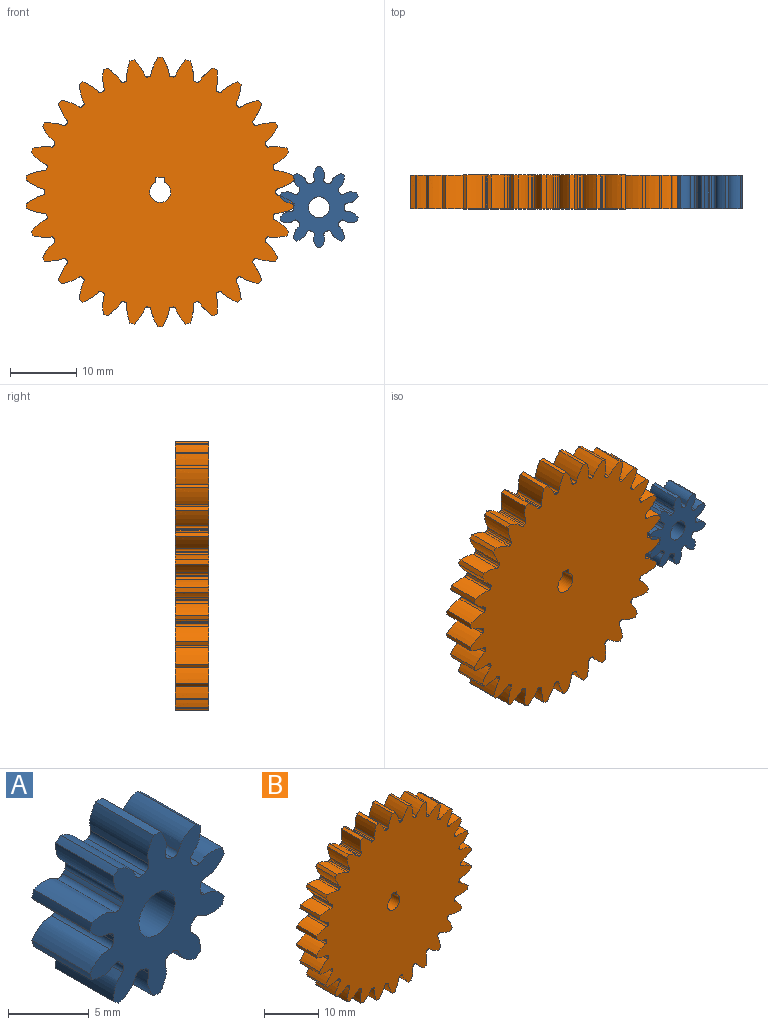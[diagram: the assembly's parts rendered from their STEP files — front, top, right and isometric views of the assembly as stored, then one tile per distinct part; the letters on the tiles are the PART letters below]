
ASSEMBLY  parts=2 mates=1
PART A: 63 faces, bbox 11.8x5.1x12.2 mm
  f0: cylinder r=6.1mm len=5.08mm, axis (0,1,0), area 3mm2, adj f9,f11,f52,f59
  f1: cylinder r=6.1mm len=5.08mm, axis (0,1,0), area 3mm2, adj f9,f11,f12,f54
  f2: cylinder r=6.1mm len=5.08mm, axis (0,1,0), area 3mm2, adj f9,f11,f42,f49
  f3: cylinder r=6.1mm len=5.08mm, axis (0,1,0), area 3mm2, adj f9,f11,f44,f57
  f4: cylinder r=6.1mm len=5.08mm, axis (0,1,0), area 3mm2, adj f9,f11,f32,f39
  f5: cylinder r=6.1mm len=5.08mm, axis (0,1,0), area 3mm2, adj f9,f11,f27,f34
  f6: cylinder r=6.1mm len=5.08mm, axis (0,1,0), area 3mm2, adj f9,f11,f22,f29
  f7: cylinder r=6.1mm len=5.08mm, axis (0,1,0), area 3mm2, adj f9,f11,f24,f47
  f8: cylinder r=6.1mm len=5.08mm, axis (0,1,0), area 3mm2, adj f9,f11,f19,f37
  f9: plane 12.21x11.79mm, normal (0,-1,0), area 69.6mm2, adj f0,f1,f2,f3,f4,f5,f6,f7
  f10: cylinder r=6.1mm len=5.08mm, axis (0,1,0), area 3mm2, adj f9,f11,f14,f17
  f11: plane 12.21x11.79mm, normal (0,1,0), area 69.6mm2, adj f0,f1,f2,f3,f4,f5,f6,f7
  f12: extruded ~5.08x1.72mm, area 10.5mm2, adj f1,f9,f11,f15
  f13: cylinder r=3.81mm len=5.08mm, axis (0,1,0), area 1.7mm2, adj f9,f11,f15,f16
  f14: extruded ~5.08x1.72mm, area 10.5mm2, adj f9,f10,f11,f16
  f15: cylinder r=0.42mm len=5.08mm, axis (0,1,0), area 3.1mm2, adj f9,f11,f12,f13
  f16: cylinder r=0.42mm len=5.08mm, axis (0,1,0), area 3.1mm2, adj f9,f11,f13,f14
  f17: extruded ~5.08x1.98mm, area 10.5mm2, adj f9,f10,f11,f20
  f18: cylinder r=3.81mm len=5.08mm, axis (0,1,0), area 1.7mm2, adj f9,f11,f20,f21
  f19: extruded ~5.08x1.82mm, area 10.5mm2, adj f8,f9,f11,f21
  f20: cylinder r=0.42mm len=5.08mm, axis (0,1,0), area 3.1mm2, adj f9,f11,f17,f18
  f21: cylinder r=0.42mm len=5.08mm, axis (0,1,0), area 3.1mm2, adj f9,f11,f18,f19
  f22: extruded ~5.08x1.72mm, area 10.5mm2, adj f6,f9,f11,f25
  f23: cylinder r=3.81mm len=5.08mm, axis (0,1,0), area 1.7mm2, adj f9,f11,f25,f26
  f24: extruded ~5.08x1.72mm, area 10.5mm2, adj f7,f9,f11,f26
  f25: cylinder r=0.42mm len=5.08mm, axis (0,1,0), area 3.1mm2, adj f9,f11,f22,f23
  f26: cylinder r=0.42mm len=5.08mm, axis (0,1,0), area 3.1mm2, adj f9,f11,f23,f24
  f27: extruded ~5.08x1.82mm, area 10.5mm2, adj f5,f9,f11,f30
  f28: cylinder r=3.81mm len=5.08mm, axis (0,1,0), area 1.7mm2, adj f9,f11,f30,f31
  f29: extruded ~5.08x1.98mm, area 10.5mm2, adj f6,f9,f11,f31
  f30: cylinder r=0.42mm len=5.08mm, axis (0,1,0), area 3.1mm2, adj f9,f11,f27,f28
  f31: cylinder r=0.42mm len=5.08mm, axis (0,1,0), area 3.1mm2, adj f9,f11,f28,f29
  f32: extruded ~5.08x1.94mm, area 10.5mm2, adj f4,f9,f11,f35
  f33: cylinder r=3.81mm len=5.08mm, axis (0,1,0), area 1.7mm2, adj f9,f11,f35,f36
  f34: extruded ~5.08x1.48mm, area 10.5mm2, adj f5,f9,f11,f36
  f35: cylinder r=0.42mm len=5.08mm, axis (0,1,0), area 3.1mm2, adj f9,f11,f32,f33
  f36: cylinder r=0.42mm len=5.08mm, axis (0,1,0), area 3.1mm2, adj f9,f11,f33,f34
  f37: extruded ~5.08x1.48mm, area 10.5mm2, adj f8,f9,f11,f40
  f38: cylinder r=3.81mm len=5.08mm, axis (0,1,0), area 1.7mm2, adj f9,f11,f40,f41
  f39: extruded ~5.08x1.94mm, area 10.5mm2, adj f4,f9,f11,f41
  f40: cylinder r=0.42mm len=5.08mm, axis (0,1,0), area 3.1mm2, adj f9,f11,f37,f38
  f41: cylinder r=0.42mm len=5.08mm, axis (0,1,0), area 3.1mm2, adj f9,f11,f38,f39
  f42: extruded ~5.08x1.48mm, area 10.5mm2, adj f2,f9,f11,f45
  f43: cylinder r=3.81mm len=5.08mm, axis (0,1,0), area 1.7mm2, adj f9,f11,f45,f46
  f44: extruded ~5.08x1.94mm, area 10.5mm2, adj f3,f9,f11,f46
  f45: cylinder r=0.42mm len=5.08mm, axis (0,1,0), area 3.1mm2, adj f9,f11,f42,f43
  f46: cylinder r=0.42mm len=5.08mm, axis (0,1,0), area 3.1mm2, adj f9,f11,f43,f44
  f47: extruded ~5.08x1.98mm, area 10.5mm2, adj f7,f9,f11,f50
  f48: cylinder r=3.81mm len=5.08mm, axis (0,1,0), area 1.7mm2, adj f9,f11,f50,f51
  f49: extruded ~5.08x1.82mm, area 10.5mm2, adj f2,f9,f11,f51
  f50: cylinder r=0.42mm len=5.08mm, axis (0,1,0), area 3.1mm2, adj f9,f11,f47,f48
  f51: cylinder r=0.42mm len=5.08mm, axis (0,1,0), area 3.1mm2, adj f9,f11,f48,f49
  f52: extruded ~5.08x1.82mm, area 10.5mm2, adj f0,f9,f11,f55
  f53: cylinder r=3.81mm len=5.08mm, axis (0,1,0), area 1.7mm2, adj f9,f11,f55,f56
  f54: extruded ~5.08x1.98mm, area 10.5mm2, adj f1,f9,f11,f56
  f55: cylinder r=0.42mm len=5.08mm, axis (0,1,0), area 3.1mm2, adj f9,f11,f52,f53
  f56: cylinder r=0.42mm len=5.08mm, axis (0,1,0), area 3.1mm2, adj f9,f11,f53,f54
  f57: extruded ~5.08x1.94mm, area 10.5mm2, adj f3,f9,f11,f60
  f58: cylinder r=3.81mm len=5.08mm, axis (0,1,0), area 1.7mm2, adj f9,f11,f60,f61
  f59: extruded ~5.08x1.48mm, area 10.5mm2, adj f0,f9,f11,f61
  f60: cylinder r=0.42mm len=5.08mm, axis (0,1,0), area 3.1mm2, adj f9,f11,f57,f58
  f61: cylinder r=0.42mm len=5.08mm, axis (0,1,0), area 3.1mm2, adj f9,f11,f58,f59
  f62: cylinder r=1.59mm len=5.08mm, axis (0,1,0), area 50.7mm2, adj f9,f11
PART B: 186 faces, bbox 40.5x5.1x40.6 mm
  f0: cylinder r=20.32mm len=5.08mm, axis (0,1,0), area 3.5mm2, adj f29,f35,f176,f183
  f1: cylinder r=20.32mm len=5.08mm, axis (0,1,0), area 3.5mm2, adj f29,f35,f171,f178
  f2: cylinder r=20.32mm len=5.08mm, axis (0,1,0), area 3.5mm2, adj f29,f35,f166,f173
  f3: cylinder r=20.32mm len=5.08mm, axis (0,1,0), area 3.5mm2, adj f29,f35,f156,f168
  f4: cylinder r=20.32mm len=5.08mm, axis (0,1,0), area 3.5mm2, adj f29,f35,f151,f163
  f5: cylinder r=20.32mm len=5.08mm, axis (0,1,0), area 3.5mm2, adj f29,f35,f158,f161
  f6: cylinder r=20.32mm len=5.08mm, axis (0,1,0), area 3.5mm2, adj f29,f35,f146,f153
  f7: cylinder r=20.32mm len=5.08mm, axis (0,1,0), area 3.5mm2, adj f29,f35,f36,f148
  f8: cylinder r=20.32mm len=5.08mm, axis (0,1,0), area 3.5mm2, adj f29,f35,f131,f143
  f9: cylinder r=20.32mm len=5.08mm, axis (0,1,0), area 3.5mm2, adj f29,f35,f138,f141
  f10: cylinder r=20.32mm len=5.08mm, axis (0,1,0), area 3.5mm2, adj f29,f35,f126,f133
  f11: cylinder r=20.32mm len=5.08mm, axis (0,1,0), area 3.5mm2, adj f29,f35,f128,f181
  f12: cylinder r=20.32mm len=5.08mm, axis (0,1,0), area 3.5mm2, adj f29,f35,f123,f136
  f13: cylinder r=20.32mm len=5.08mm, axis (0,1,0), area 3.5mm2, adj f29,f35,f118,f121
  f14: cylinder r=20.32mm len=5.08mm, axis (0,1,0), area 3.5mm2, adj f29,f35,f113,f116
  f15: cylinder r=20.32mm len=5.08mm, axis (0,1,0), area 3.5mm2, adj f29,f35,f108,f111
  f16: cylinder r=20.32mm len=5.08mm, axis (0,1,0), area 3.5mm2, adj f29,f35,f91,f103
  f17: cylinder r=20.32mm len=5.08mm, axis (0,1,0), area 3.5mm2, adj f29,f35,f98,f101
  f18: cylinder r=20.32mm len=5.08mm, axis (0,1,0), area 3.5mm2, adj f29,f35,f86,f93
  f19: cylinder r=20.32mm len=5.08mm, axis (0,1,0), area 3.5mm2, adj f29,f35,f88,f106
  f20: cylinder r=20.32mm len=5.08mm, axis (0,1,0), area 3.5mm2, adj f29,f35,f83,f96
  f21: cylinder r=20.32mm len=5.08mm, axis (0,1,0), area 3.5mm2, adj f29,f35,f78,f81
  f22: cylinder r=20.32mm len=5.08mm, axis (0,1,0), area 3.5mm2, adj f29,f35,f73,f76
  f23: cylinder r=20.32mm len=5.08mm, axis (0,1,0), area 3.5mm2, adj f29,f35,f68,f71
  f24: cylinder r=20.32mm len=5.08mm, axis (0,1,0), area 3.5mm2, adj f29,f35,f56,f63
  f25: cylinder r=20.32mm len=5.08mm, axis (0,1,0), area 3.5mm2, adj f29,f35,f46,f58
  f26: cylinder r=20.32mm len=5.08mm, axis (0,1,0), area 3.5mm2, adj f29,f35,f53,f66
  f27: cylinder r=20.32mm len=5.08mm, axis (0,1,0), area 3.5mm2, adj f29,f35,f48,f51
  f28: cylinder r=20.32mm len=5.08mm, axis (0,1,0), area 3.5mm2, adj f29,f35,f43,f61
  f29: plane 40.64x40.49mm, normal (0,-1,0), area 1122.1mm2, adj f0,f1,f2,f3,f4,f5,f6,f7
  f30: plane 5.08x0.77mm, normal (-1,0,0), area 3.9mm2, adj f29,f31,f33,f35
  f31: cylinder r=1.59mm len=5.08mm, axis (0,1,0), area 44mm2, adj f29,f30,f32,f35
  f32: plane 5.08x0.77mm, normal (1,0,0), area 3.9mm2, adj f29,f31,f33,f35
  f33: plane 5.08x1.27mm, normal (0,0,-1), area 6.5mm2, adj f29,f30,f32,f35
  f34: cylinder r=20.32mm len=5.08mm, axis (0,1,0), area 3.5mm2, adj f29,f35,f38,f41
  f35: plane 40.64x40.49mm, normal (0,1,0), area 1122.1mm2, adj f0,f1,f2,f3,f4,f5,f6,f7
  f36: extruded ~5.08x2.52mm, area 14.5mm2, adj f7,f29,f35,f39
  f37: cylinder r=17.46mm len=5.08mm, axis (0,1,0), area 1.3mm2, adj f29,f35,f39,f40
  f38: extruded ~5.08x2.52mm, area 14.5mm2, adj f29,f34,f35,f40
  f39: cylinder r=0.35mm len=5.08mm, axis (0,1,0), area 2.3mm2, adj f29,f35,f36,f37
  f40: cylinder r=0.35mm len=5.08mm, axis (0,1,0), area 2.3mm2, adj f29,f35,f37,f38
  f41: extruded ~5.08x2.74mm, area 14.5mm2, adj f29,f34,f35,f44
  f42: cylinder r=17.46mm len=5.08mm, axis (0,1,0), area 1.3mm2, adj f29,f35,f44,f45
  f43: extruded ~5.08x2.19mm, area 14.5mm2, adj f28,f29,f35,f45
  f44: cylinder r=0.35mm len=5.08mm, axis (0,1,0), area 2.3mm2, adj f29,f35,f41,f42
  f45: cylinder r=0.35mm len=5.08mm, axis (0,1,0), area 2.3mm2, adj f29,f35,f42,f43
  f46: extruded ~5.08x2.66mm, area 14.5mm2, adj f25,f29,f35,f49
  f47: cylinder r=17.46mm len=5.08mm, axis (0,1,0), area 1.3mm2, adj f29,f35,f49,f50
  f48: extruded ~5.08x2.75mm, area 14.5mm2, adj f27,f29,f35,f50
  f49: cylinder r=0.35mm len=5.08mm, axis (0,1,0), area 2.3mm2, adj f29,f35,f46,f47
  f50: cylinder r=0.35mm len=5.08mm, axis (0,1,0), area 2.3mm2, adj f29,f35,f47,f48
  f51: extruded ~5.08x2.39mm, area 14.5mm2, adj f27,f29,f35,f54
  f52: cylinder r=17.46mm len=5.08mm, axis (0,1,0), area 1.3mm2, adj f29,f35,f54,f55
  f53: extruded ~5.08x2.84mm, area 14.5mm2, adj f26,f29,f35,f55
  f54: cylinder r=0.35mm len=5.08mm, axis (0,1,0), area 2.3mm2, adj f29,f35,f51,f52
  f55: cylinder r=0.35mm len=5.08mm, axis (0,1,0), area 2.3mm2, adj f29,f35,f52,f53
  f56: extruded ~5.08x2.81mm, area 14.5mm2, adj f24,f29,f35,f59
  f57: cylinder r=17.46mm len=5.08mm, axis (0,1,0), area 1.3mm2, adj f29,f35,f59,f60
  f58: extruded ~5.08x2.54mm, area 14.5mm2, adj f25,f29,f35,f60
  f59: cylinder r=0.35mm len=5.08mm, axis (0,1,0), area 2.3mm2, adj f29,f35,f56,f57
  f60: cylinder r=0.35mm len=5.08mm, axis (0,1,0), area 2.3mm2, adj f29,f35,f57,f58
  f61: extruded ~5.08x2.83mm, area 14.5mm2, adj f28,f29,f35,f64
  f62: cylinder r=17.46mm len=5.08mm, axis (0,1,0), area 1.3mm2, adj f29,f35,f64,f65
  f63: extruded ~5.08x2.22mm, area 14.5mm2, adj f24,f29,f35,f65
  f64: cylinder r=0.35mm len=5.08mm, axis (0,1,0), area 2.3mm2, adj f29,f35,f61,f62
  f65: cylinder r=0.35mm len=5.08mm, axis (0,1,0), area 2.3mm2, adj f29,f35,f62,f63
  f66: extruded ~5.08x2.02mm, area 14.5mm2, adj f26,f29,f35,f69
  f67: cylinder r=17.46mm len=5.08mm, axis (0,1,0), area 1.3mm2, adj f29,f35,f69,f70
  f68: extruded ~5.08x2.8mm, area 14.5mm2, adj f23,f29,f35,f70
  f69: cylinder r=0.35mm len=5.08mm, axis (0,1,0), area 2.3mm2, adj f29,f35,f66,f67
  f70: cylinder r=0.35mm len=5.08mm, axis (0,1,0), area 2.3mm2, adj f29,f35,f67,f68
  f71: extruded ~5.08x2.37mm, area 14.5mm2, adj f23,f29,f35,f74
  f72: cylinder r=17.46mm len=5.08mm, axis (0,1,0), area 1.3mm2, adj f29,f35,f74,f75
  f73: extruded ~5.08x2.64mm, area 14.5mm2, adj f22,f29,f35,f75
  f74: cylinder r=0.35mm len=5.08mm, axis (0,1,0), area 2.3mm2, adj f29,f35,f71,f72
  f75: cylinder r=0.35mm len=5.08mm, axis (0,1,0), area 2.3mm2, adj f29,f35,f72,f73
  f76: extruded ~5.08x2.64mm, area 14.5mm2, adj f22,f29,f35,f79
  f77: cylinder r=17.46mm len=5.08mm, axis (0,1,0), area 1.3mm2, adj f29,f35,f79,f80
  f78: extruded ~5.08x2.37mm, area 14.5mm2, adj f21,f29,f35,f80
  f79: cylinder r=0.35mm len=5.08mm, axis (0,1,0), area 2.3mm2, adj f29,f35,f76,f77
  f80: cylinder r=0.35mm len=5.08mm, axis (0,1,0), area 2.3mm2, adj f29,f35,f77,f78
  f81: extruded ~5.08x2.8mm, area 14.5mm2, adj f21,f29,f35,f84
  f82: cylinder r=17.46mm len=5.08mm, axis (0,1,0), area 1.3mm2, adj f29,f35,f84,f85
  f83: extruded ~5.08x2.02mm, area 14.5mm2, adj f20,f29,f35,f85
  f84: cylinder r=0.35mm len=5.08mm, axis (0,1,0), area 2.3mm2, adj f29,f35,f81,f82
  f85: cylinder r=0.35mm len=5.08mm, axis (0,1,0), area 2.3mm2, adj f29,f35,f82,f83
  f86: extruded ~5.08x2.22mm, area 14.5mm2, adj f18,f29,f35,f89
  f87: cylinder r=17.46mm len=5.08mm, axis (0,1,0), area 1.3mm2, adj f29,f35,f89,f90
  f88: extruded ~5.08x2.83mm, area 14.5mm2, adj f19,f29,f35,f90
  f89: cylinder r=0.35mm len=5.08mm, axis (0,1,0), area 2.3mm2, adj f29,f35,f86,f87
  f90: cylinder r=0.35mm len=5.08mm, axis (0,1,0), area 2.3mm2, adj f29,f35,f87,f88
  f91: extruded ~5.08x2.54mm, area 14.5mm2, adj f16,f29,f35,f94
  f92: cylinder r=17.46mm len=5.08mm, axis (0,1,0), area 1.3mm2, adj f29,f35,f94,f95
  f93: extruded ~5.08x2.81mm, area 14.5mm2, adj f18,f29,f35,f95
  f94: cylinder r=0.35mm len=5.08mm, axis (0,1,0), area 2.3mm2, adj f29,f35,f91,f92
  f95: cylinder r=0.35mm len=5.08mm, axis (0,1,0), area 2.3mm2, adj f29,f35,f92,f93
  f96: extruded ~5.08x2.84mm, area 14.5mm2, adj f20,f29,f35,f99
  f97: cylinder r=17.46mm len=5.08mm, axis (0,1,0), area 1.3mm2, adj f29,f35,f99,f100
  f98: extruded ~5.08x2.39mm, area 14.5mm2, adj f17,f29,f35,f100
  f99: cylinder r=0.35mm len=5.08mm, axis (0,1,0), area 2.3mm2, adj f29,f35,f96,f97
  f100: cylinder r=0.35mm len=5.08mm, axis (0,1,0), area 2.3mm2, adj f29,f35,f97,f98
  f101: extruded ~5.08x2.75mm, area 14.5mm2, adj f17,f29,f35,f104
  f102: cylinder r=17.46mm len=5.08mm, axis (0,1,0), area 1.3mm2, adj f29,f35,f104,f105
  f103: extruded ~5.08x2.66mm, area 14.5mm2, adj f16,f29,f35,f105
  f104: cylinder r=0.35mm len=5.08mm, axis (0,1,0), area 2.3mm2, adj f29,f35,f101,f102
  f105: cylinder r=0.35mm len=5.08mm, axis (0,1,0), area 2.3mm2, adj f29,f35,f102,f103
  f106: extruded ~5.08x2.19mm, area 14.5mm2, adj f19,f29,f35,f109
  f107: cylinder r=17.46mm len=5.08mm, axis (0,1,0), area 1.3mm2, adj f29,f35,f109,f110
  f108: extruded ~5.08x2.74mm, area 14.5mm2, adj f15,f29,f35,f110
  f109: cylinder r=0.35mm len=5.08mm, axis (0,1,0), area 2.3mm2, adj f29,f35,f106,f107
  f110: cylinder r=0.35mm len=5.08mm, axis (0,1,0), area 2.3mm2, adj f29,f35,f107,f108
  f111: extruded ~5.08x2.52mm, area 14.5mm2, adj f15,f29,f35,f114
  f112: cylinder r=17.46mm len=5.08mm, axis (0,1,0), area 1.3mm2, adj f29,f35,f114,f115
  f113: extruded ~5.08x2.52mm, area 14.5mm2, adj f14,f29,f35,f115
  f114: cylinder r=0.35mm len=5.08mm, axis (0,1,0), area 2.3mm2, adj f29,f35,f111,f112
  f115: cylinder r=0.35mm len=5.08mm, axis (0,1,0), area 2.3mm2, adj f29,f35,f112,f113
  f116: extruded ~5.08x2.74mm, area 14.5mm2, adj f14,f29,f35,f119
  f117: cylinder r=17.46mm len=5.08mm, axis (0,1,0), area 1.3mm2, adj f29,f35,f119,f120
  f118: extruded ~5.08x2.19mm, area 14.5mm2, adj f13,f29,f35,f120
  f119: cylinder r=0.35mm len=5.08mm, axis (0,1,0), area 2.3mm2, adj f29,f35,f116,f117
  f120: cylinder r=0.35mm len=5.08mm, axis (0,1,0), area 2.3mm2, adj f29,f35,f117,f118
  f121: extruded ~5.08x2.83mm, area 14.5mm2, adj f13,f29,f35,f124
  f122: cylinder r=17.46mm len=5.08mm, axis (0,1,0), area 1.3mm2, adj f29,f35,f124,f125
  f123: extruded ~5.08x2.22mm, area 14.5mm2, adj f12,f29,f35,f125
  f124: cylinder r=0.35mm len=5.08mm, axis (0,1,0), area 2.3mm2, adj f29,f35,f121,f122
  f125: cylinder r=0.35mm len=5.08mm, axis (0,1,0), area 2.3mm2, adj f29,f35,f122,f123
  f126: extruded ~5.08x2.02mm, area 14.5mm2, adj f10,f29,f35,f129
  f127: cylinder r=17.46mm len=5.08mm, axis (0,1,0), area 1.3mm2, adj f29,f35,f129,f130
  f128: extruded ~5.08x2.8mm, area 14.5mm2, adj f11,f29,f35,f130
  f129: cylinder r=0.35mm len=5.08mm, axis (0,1,0), area 2.3mm2, adj f29,f35,f126,f127
  f130: cylinder r=0.35mm len=5.08mm, axis (0,1,0), area 2.3mm2, adj f29,f35,f127,f128
  f131: extruded ~5.08x2.39mm, area 14.5mm2, adj f8,f29,f35,f134
  f132: cylinder r=17.46mm len=5.08mm, axis (0,1,0), area 1.3mm2, adj f29,f35,f134,f135
  f133: extruded ~5.08x2.84mm, area 14.5mm2, adj f10,f29,f35,f135
  f134: cylinder r=0.35mm len=5.08mm, axis (0,1,0), area 2.3mm2, adj f29,f35,f131,f132
  f135: cylinder r=0.35mm len=5.08mm, axis (0,1,0), area 2.3mm2, adj f29,f35,f132,f133
  f136: extruded ~5.08x2.81mm, area 14.5mm2, adj f12,f29,f35,f139
  f137: cylinder r=17.46mm len=5.08mm, axis (0,1,0), area 1.3mm2, adj f29,f35,f139,f140
  f138: extruded ~5.08x2.54mm, area 14.5mm2, adj f9,f29,f35,f140
  f139: cylinder r=0.35mm len=5.08mm, axis (0,1,0), area 2.3mm2, adj f29,f35,f136,f137
  f140: cylinder r=0.35mm len=5.08mm, axis (0,1,0), area 2.3mm2, adj f29,f35,f137,f138
  f141: extruded ~5.08x2.66mm, area 14.5mm2, adj f9,f29,f35,f144
  f142: cylinder r=17.46mm len=5.08mm, axis (0,1,0), area 1.3mm2, adj f29,f35,f144,f145
  f143: extruded ~5.08x2.75mm, area 14.5mm2, adj f8,f29,f35,f145
  f144: cylinder r=0.35mm len=5.08mm, axis (0,1,0), area 2.3mm2, adj f29,f35,f141,f142
  f145: cylinder r=0.35mm len=5.08mm, axis (0,1,0), area 2.3mm2, adj f29,f35,f142,f143
  f146: extruded ~5.08x2.19mm, area 14.5mm2, adj f6,f29,f35,f149
  f147: cylinder r=17.46mm len=5.08mm, axis (0,1,0), area 1.3mm2, adj f29,f35,f149,f150
  f148: extruded ~5.08x2.74mm, area 14.5mm2, adj f7,f29,f35,f150
  f149: cylinder r=0.35mm len=5.08mm, axis (0,1,0), area 2.3mm2, adj f29,f35,f146,f147
  f150: cylinder r=0.35mm len=5.08mm, axis (0,1,0), area 2.3mm2, adj f29,f35,f147,f148
  f151: extruded ~5.08x2.22mm, area 14.5mm2, adj f4,f29,f35,f154
  f152: cylinder r=17.46mm len=5.08mm, axis (0,1,0), area 1.3mm2, adj f29,f35,f154,f155
  f153: extruded ~5.08x2.83mm, area 14.5mm2, adj f6,f29,f35,f155
  f154: cylinder r=0.35mm len=5.08mm, axis (0,1,0), area 2.3mm2, adj f29,f35,f151,f152
  f155: cylinder r=0.35mm len=5.08mm, axis (0,1,0), area 2.3mm2, adj f29,f35,f152,f153
  f156: extruded ~5.08x2.75mm, area 14.5mm2, adj f3,f29,f35,f159
  f157: cylinder r=17.46mm len=5.08mm, axis (0,1,0), area 1.3mm2, adj f29,f35,f159,f160
  f158: extruded ~5.08x2.66mm, area 14.5mm2, adj f5,f29,f35,f160
  f159: cylinder r=0.35mm len=5.08mm, axis (0,1,0), area 2.3mm2, adj f29,f35,f156,f157
  f160: cylinder r=0.35mm len=5.08mm, axis (0,1,0), area 2.3mm2, adj f29,f35,f157,f158
  f161: extruded ~5.08x2.54mm, area 14.5mm2, adj f5,f29,f35,f164
  f162: cylinder r=17.46mm len=5.08mm, axis (0,1,0), area 1.3mm2, adj f29,f35,f164,f165
  f163: extruded ~5.08x2.81mm, area 14.5mm2, adj f4,f29,f35,f165
  f164: cylinder r=0.35mm len=5.08mm, axis (0,1,0), area 2.3mm2, adj f29,f35,f161,f162
  f165: cylinder r=0.35mm len=5.08mm, axis (0,1,0), area 2.3mm2, adj f29,f35,f162,f163
  f166: extruded ~5.08x2.84mm, area 14.5mm2, adj f2,f29,f35,f169
  f167: cylinder r=17.46mm len=5.08mm, axis (0,1,0), area 1.3mm2, adj f29,f35,f169,f170
  f168: extruded ~5.08x2.39mm, area 14.5mm2, adj f3,f29,f35,f170
  f169: cylinder r=0.35mm len=5.08mm, axis (0,1,0), area 2.3mm2, adj f29,f35,f166,f167
  f170: cylinder r=0.35mm len=5.08mm, axis (0,1,0), area 2.3mm2, adj f29,f35,f167,f168
  f171: extruded ~5.08x2.8mm, area 14.5mm2, adj f1,f29,f35,f174
  f172: cylinder r=17.46mm len=5.08mm, axis (0,1,0), area 1.3mm2, adj f29,f35,f174,f175
  f173: extruded ~5.08x2.02mm, area 14.5mm2, adj f2,f29,f35,f175
  f174: cylinder r=0.35mm len=5.08mm, axis (0,1,0), area 2.3mm2, adj f29,f35,f171,f172
  f175: cylinder r=0.35mm len=5.08mm, axis (0,1,0), area 2.3mm2, adj f29,f35,f172,f173
  f176: extruded ~5.08x2.64mm, area 14.5mm2, adj f0,f29,f35,f179
  f177: cylinder r=17.46mm len=5.08mm, axis (0,1,0), area 1.3mm2, adj f29,f35,f179,f180
  f178: extruded ~5.08x2.37mm, area 14.5mm2, adj f1,f29,f35,f180
  f179: cylinder r=0.35mm len=5.08mm, axis (0,1,0), area 2.3mm2, adj f29,f35,f176,f177
  f180: cylinder r=0.35mm len=5.08mm, axis (0,1,0), area 2.3mm2, adj f29,f35,f177,f178
  f181: extruded ~5.08x2.37mm, area 14.5mm2, adj f11,f29,f35,f184
  f182: cylinder r=17.46mm len=5.08mm, axis (0,1,0), area 1.3mm2, adj f29,f35,f184,f185
  f183: extruded ~5.08x2.64mm, area 14.5mm2, adj f0,f29,f35,f185
  f184: cylinder r=0.35mm len=5.08mm, axis (0,1,0), area 2.3mm2, adj f29,f35,f181,f182
  f185: cylinder r=0.35mm len=5.08mm, axis (0,1,0), area 2.3mm2, adj f29,f35,f182,f183
PLACE A t=(2.4,6.37,-6.78)mm
PLACE B t=(-21.58,6.37,-4.47)mm
MATE revolute B.f29 <-> A.f9  axis (0,-1,0) through (-1.41,1.29,-6.94)mm
